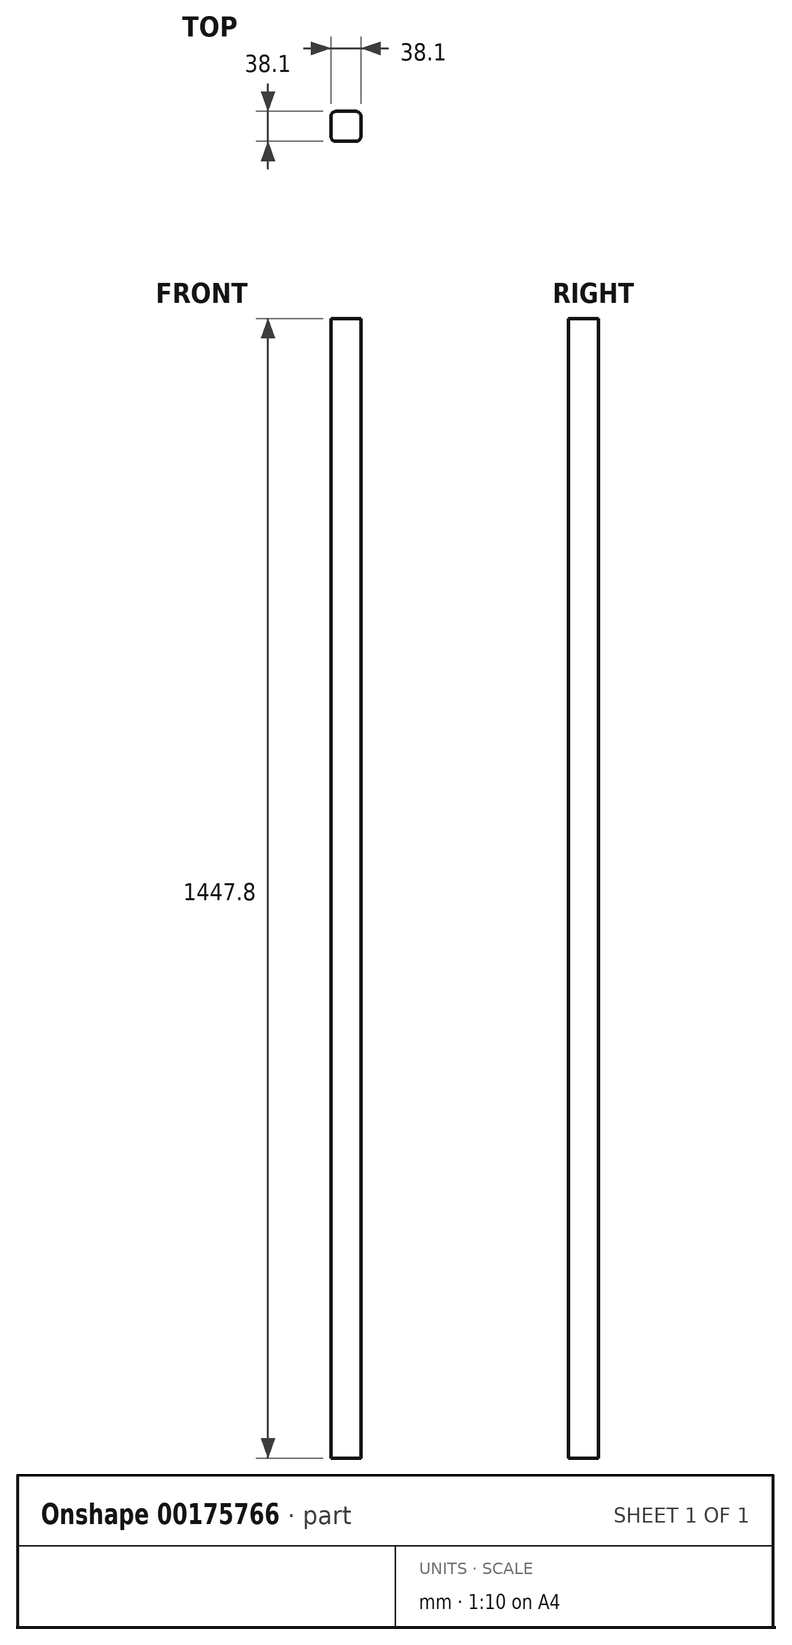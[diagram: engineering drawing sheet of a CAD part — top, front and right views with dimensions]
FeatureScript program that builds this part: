
annotation { "Feature Type Name" : "Feature", "Feature Type Description" : "" }
export const myFeature = defineFeature(function(context is Context, id is Id, definition is map)
    precondition{}
    {
        {
            var Q0;
            Q0=qCreatedBy(makeId("Top.planeOp"),FACE);
            var sketch = newSketch(context, id + "F0", { "sketchPlane" : qUnion([Q0])});
            skLineSegment(sketch, "E0.bottom", {"start": v(12.7, 19.05) * mm, "end": v(-12.7, 19.05) * mm});
            skLineSegment(sketch, "E0.top", {"start": v(12.7, -19.05) * mm, "end": v(-12.7, -19.05) * mm});
            skLineSegment(sketch, "E0.left", {"start": v(19.05, 12.7) * mm, "end": v(19.05, -12.7) * mm});
            skLineSegment(sketch, "E0.right", {"start": v(-19.05, 12.7) * mm, "end": v(-19.05, -12.7) * mm});
            skPoint(sketch, "E0.middle", {"position": v(0, 0) * mm});
            skPoint(sketch, "E1.visualSharp", {"position": v(-19.05, 19.05) * mm});
            skPoint(sketch, "E2.visualSharp", {"position": v(19.05, 19.05) * mm});
            skArc(sketch, "E2.filletArc", {"start": v(19.05, 12.7) * mm, "mid": v(17.2, 17.2) * mm, "end": v(12.7, 19.05) * mm});
            skPoint(sketch, "E3.visualSharp", {"position": v(19.05, -19.05) * mm});
            skArc(sketch, "E3.filletArc", {"start": v(12.7, -19.05) * mm, "mid": v(17.2, -17.2) * mm, "end": v(19.05, -12.7) * mm});
            skPoint(sketch, "E4.visualSharp", {"position": v(-19.05, -19.05) * mm});
            skArc(sketch, "E4.filletArc", {"start": v(-19.05, -12.7) * mm, "mid": v(-17.2, -17.2) * mm, "end": v(-12.7, -19.05) * mm});
            skArc(sketch, "E5.filletArc", {"start": v(-12.7, 19.05) * mm, "mid": v(-17.2, 17.2) * mm, "end": v(-19.05, 12.7) * mm});
            skSolve(sketch);
        }
        {
            var Q0;
            Q0 = qSketchRegion(id + "F0", true);
            extrude(context, id + "F1", {"entities" : qUnion([Q0]), "depth" : 1447.8 * mm});
        }
    });
